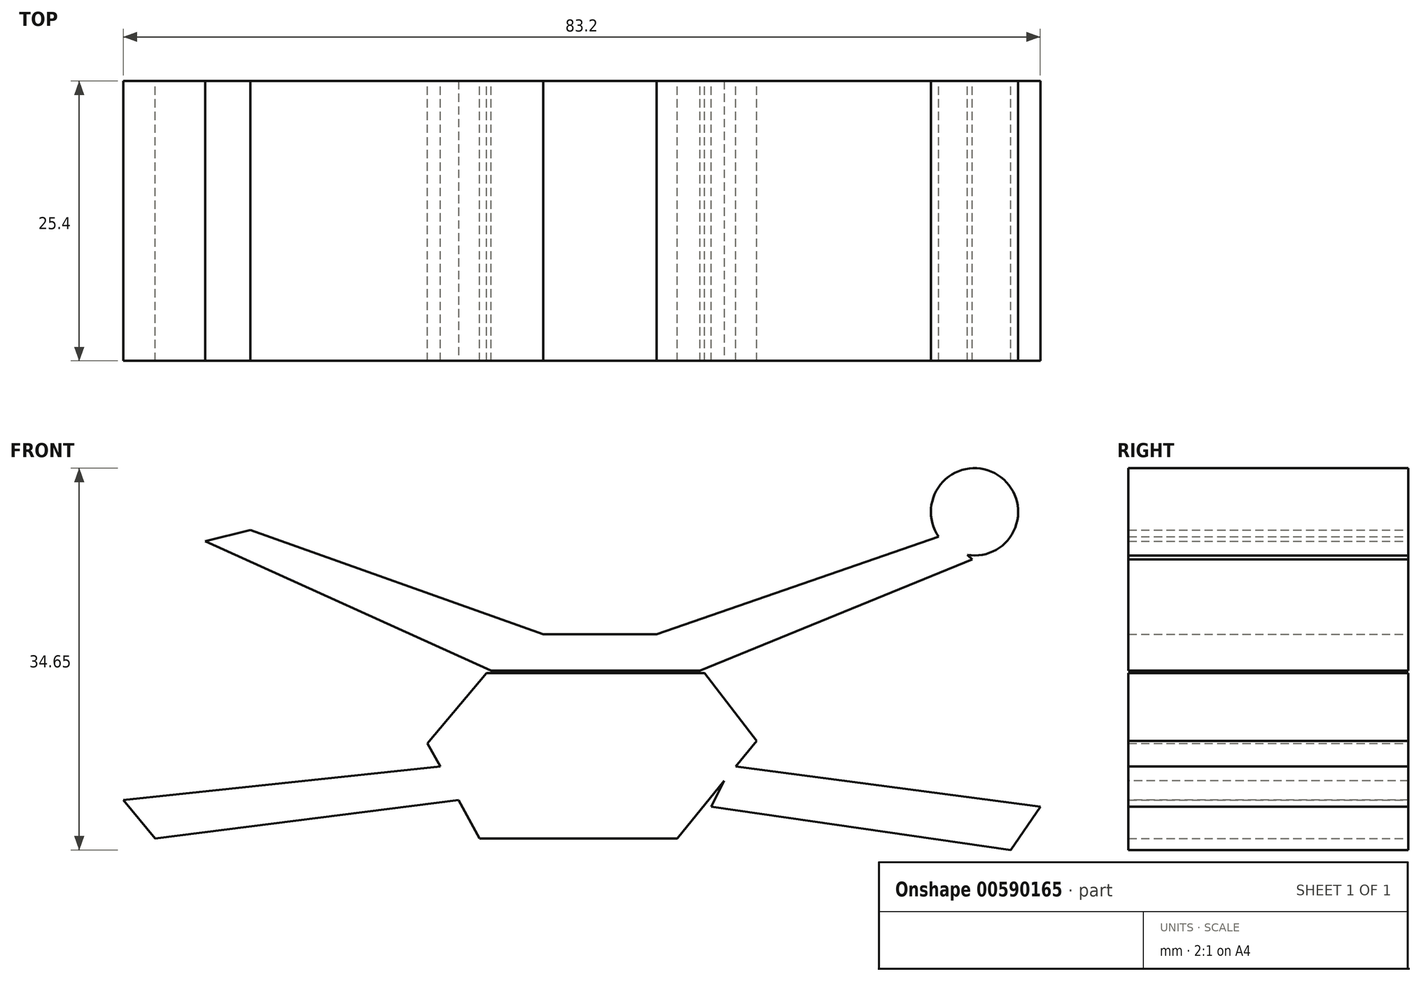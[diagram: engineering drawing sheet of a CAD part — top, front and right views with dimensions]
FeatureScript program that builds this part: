
annotation { "Feature Type Name" : "Feature", "Feature Type Description" : "" }
export const myFeature = defineFeature(function(context is Context, id is Id, definition is map)
    precondition{}
    {
        {
            var Q0;
            Q0=qCreatedBy(makeId("Front.planeOp"),FACE);
            var sketch = newSketch(context, id + "F0", { "sketchPlane" : qUnion([Q0])});
            skCircle(sketch, "E0", {"center": v(-35.94, 24.3) * mm, "radius": 4.08 * mm});
            skSolve(sketch);
        }
        {
            var Q0;
            Q0=sQuery(id+"F0.wireOp",EDGE,"E0");
            extrude(context, id + "F1", {"bodyType" : ToolBodyType.SURFACE, "surfaceEntities" : qUnion([Q0]), "depth" : 25.4 * mm, "offsetDistance" : 25.4 * mm});
        }
        {
            var Q0;
            Q0=qCreatedBy(makeId("Front.planeOp"),FACE);
            var sketch = newSketch(context, id + "F2", { "sketchPlane" : qUnion([Q0])});
            skCircle(sketch, "E1", {"center": v(33.26, 23.07) * mm, "radius": 3.96 * mm});
            skSolve(sketch);
        }
        {
            var Q0;
            Q0 = qSketchRegion(id + "F2", true);
            extrude(context, id + "F3", {"entities" : qUnion([Q0]), "depth" : 25.4 * mm, "offsetDistance" : 25.4 * mm});
        }
        {
            var Q0;
            Q0=qCreatedBy(makeId("Front.planeOp"),FACE);
            var sketch = newSketch(context, id + "F4", { "sketchPlane" : qUnion([Q0])});
            skLineSegment(sketch, "E2", {"start": v(-32.44, 21.42) * mm, "end": v(-5.87, 11.94) * mm});
            skLineSegment(sketch, "E3", {"start": v(-5.87, 11.94) * mm, "end": v(4.43, 11.94) * mm});
            skLineSegment(sketch, "E4", {"start": v(4.43, 11.94) * mm, "end": v(30.58, 21) * mm});
            skLineSegment(sketch, "E5", {"start": v(30.58, 21) * mm, "end": v(33.05, 18.74) * mm});
            skLineSegment(sketch, "E6", {"start": v(33.05, 18.74) * mm, "end": v(8.34, 8.65) * mm});
            skLineSegment(sketch, "E7", {"start": v(8.34, 8.65) * mm, "end": v(-10.6, 8.65) * mm});
            skLineSegment(sketch, "E8", {"start": v(-10.6, 8.65) * mm, "end": v(-36.56, 20.39) * mm});
            skLineSegment(sketch, "E9", {"start": v(-36.56, 20.39) * mm, "end": v(-32.44, 21.42) * mm});
            skSolve(sketch);
        }
        {
            var Q0;
            Q0 = qSketchRegion(id + "F4", true);
            extrude(context, id + "F5", {"entities" : qUnion([Q0]), "operationType" : NewBodyOperationType.ADD, "depth" : 25.4 * mm, "offsetDistance" : 25.4 * mm});
        }
        {
            var Q0;
            Q0=qCreatedBy(makeId("Front.planeOp"),FACE);
            var sketch = newSketch(context, id + "F6", { "sketchPlane" : qUnion([Q0])});
            skLineSegment(sketch, "E10", {"start": v(-11.02, 8.44) * mm, "end": v(-16.37, 2.06) * mm});
            skLineSegment(sketch, "E11", {"start": v(-16.37, 2.06) * mm, "end": v(-11.64, -6.6) * mm});
            skLineSegment(sketch, "E12", {"start": v(-11.64, -6.6) * mm, "end": v(6.28, -6.6) * mm});
            skLineSegment(sketch, "E13", {"start": v(6.28, -6.6) * mm, "end": v(13.49, 2.27) * mm});
            skLineSegment(sketch, "E14", {"start": v(13.49, 2.27) * mm, "end": v(8.75, 8.44) * mm});
            skLineSegment(sketch, "E15", {"start": v(8.75, 8.44) * mm, "end": v(-11.02, 8.44) * mm});
            skSolve(sketch);
        }
        {
            var Q0;
            Q0 = qSketchRegion(id + "F6", true);
            extrude(context, id + "F7", {"entities" : qUnion([Q0]), "depth" : 25.4 * mm, "offsetDistance" : 25.4 * mm});
        }
        {
            var Q0;
            Q0=qCreatedBy(makeId("Front.planeOp"),FACE);
            var sketch = newSketch(context, id + "F8", { "sketchPlane" : qUnion([Q0])});
            skLineSegment(sketch, "E16", {"start": v(-14.73, 0) * mm, "end": v(-43.97, -3.09) * mm});
            skLineSegment(sketch, "E17", {"start": v(-43.97, -3.09) * mm, "end": v(-41.09, -6.6) * mm});
            skLineSegment(sketch, "E18", {"start": v(-41.09, -6.6) * mm, "end": v(-13.49, -3.09) * mm});
            skLineSegment(sketch, "E19", {"start": v(-13.49, -3.09) * mm, "end": v(-14.73, 0) * mm});
            skLineSegment(sketch, "E20", {"start": v(11.43, 0) * mm, "end": v(40.88, -3.09) * mm});
            skLineSegment(sketch, "E21", {"start": v(40.88, -3.09) * mm, "end": v(38.82, -6.6) * mm});
            skLineSegment(sketch, "E22", {"start": v(38.82, -6.6) * mm, "end": v(9.37, -3.09) * mm});
            skLineSegment(sketch, "E23", {"start": v(9.37, -3.09) * mm, "end": v(-13.49, -3.09) * mm});
            skSolve(sketch);
        }
        {
            var Q0;
            Q0 = qSketchRegion(id + "F8", true);
            extrude(context, id + "F9", {"entities" : qUnion([Q0]), "operationType" : NewBodyOperationType.ADD, "depth" : 25.4 * mm, "offsetDistance" : 25.4 * mm});
        }
        {
            var Q0;
            Q0=qCreatedBy(makeId("Front.planeOp"),FACE);
            var sketch = newSketch(context, id + "F10", { "sketchPlane" : qUnion([Q0])});
            skLineSegment(sketch, "E24", {"start": v(11.22, 0) * mm, "end": v(39.23, -3.7) * mm});
            skLineSegment(sketch, "E25", {"start": v(39.23, -3.7) * mm, "end": v(36.56, -7.62) * mm});
            skLineSegment(sketch, "E26", {"start": v(36.56, -7.62) * mm, "end": v(9.37, -3.7) * mm});
            skLineSegment(sketch, "E27", {"start": v(9.37, -3.7) * mm, "end": v(11.22, 0) * mm});
            skSolve(sketch);
        }
        {
            var Q0;
            Q0 = qSketchRegion(id + "F10", true);
            extrude(context, id + "F11", {"entities" : qUnion([Q0]), "operationType" : NewBodyOperationType.ADD, "depth" : 25.4 * mm, "offsetDistance" : 25.4 * mm});
        }
    });
